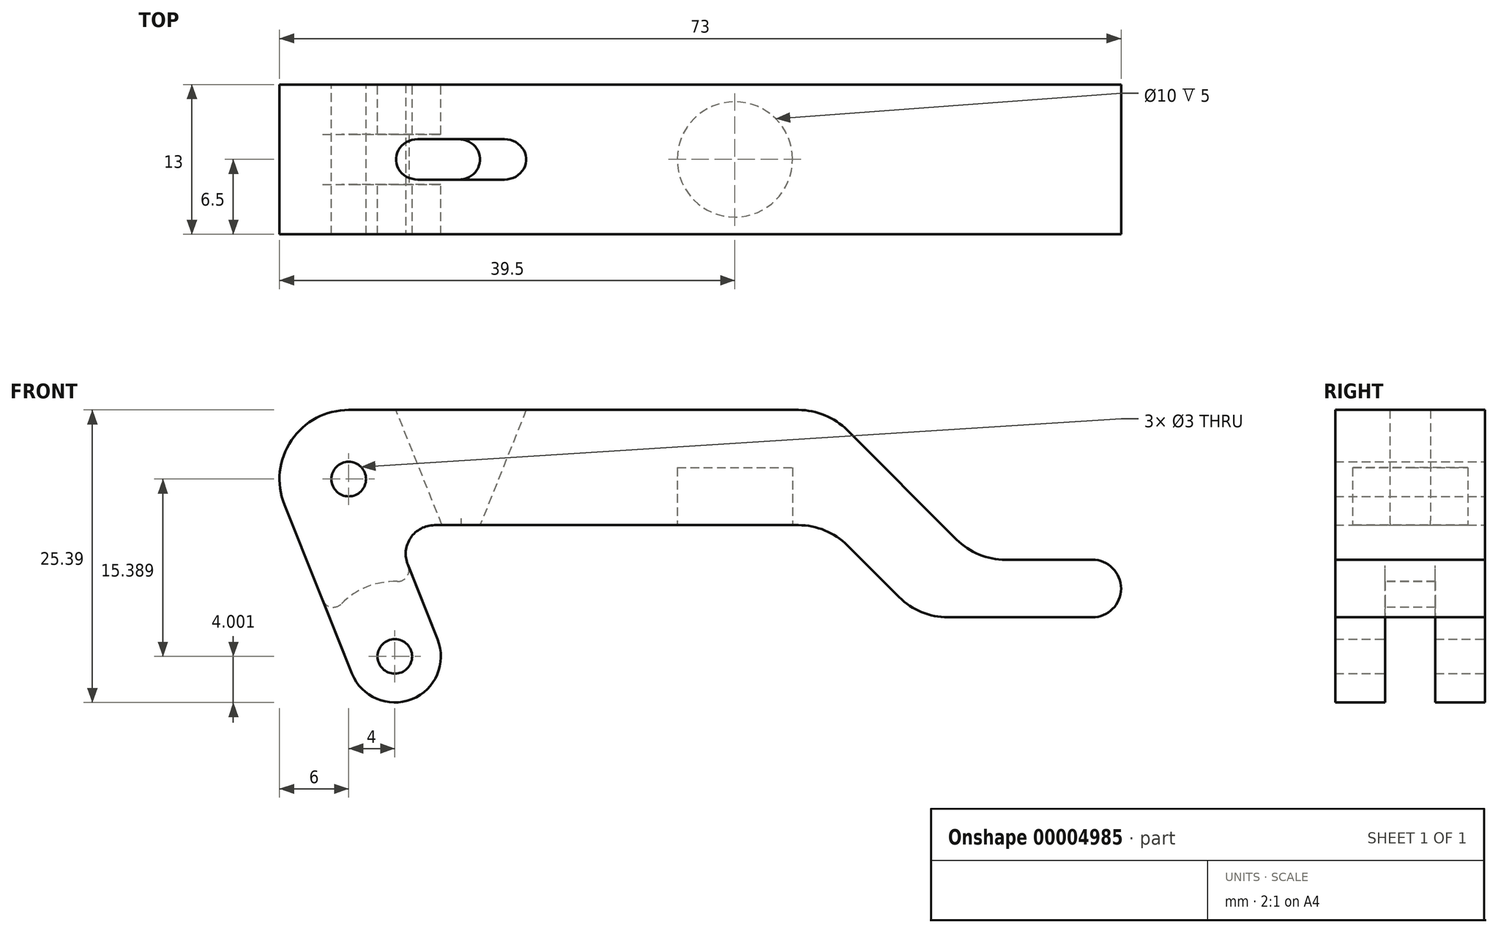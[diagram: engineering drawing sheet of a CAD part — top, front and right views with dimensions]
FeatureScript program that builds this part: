
annotation { "Feature Type Name" : "Feature", "Feature Type Description" : "" }
export const myFeature = defineFeature(function(context is Context, id is Id, definition is map)
    precondition{}
    {
        {
            var Q0;
            Q0=qCreatedBy(makeId("Front.planeOp"),FACE);
            var sketch = newSketch(context, id + "F0", { "sketchPlane" : qUnion([Q0])});
            skLineSegment(sketch, "E0", {"start": v(0, 0) * mm, "end": v(31, 0) * mm, "construction": true});
            skCircle(sketch, "E1", {"center": v(0, 0) * mm, "radius": 1.5 * mm});
            skLineSegment(sketch, "E2", {"start": v(0, 0) * mm, "end": v(4, -15.39) * mm, "construction": true});
            skCircle(sketch, "E3", {"center": v(4, -15.39) * mm, "radius": 1.5 * mm});
            skArc(sketch, "E4", {"start": v(-5.57, -2.23) * mm, "mid": v(-4.97, 3.36) * mm, "end": v(0, 6) * mm});
            skArc(sketch, "E5", {"start": v(0.29, -16.87) * mm, "mid": v(5.49, -19.1) * mm, "end": v(7.71, -13.9) * mm});
            skLineSegment(sketch, "E6", {"start": v(-5.57, -2.23) * mm, "end": v(0.29, -16.87) * mm});
            skLineSegment(sketch, "E7", {"start": v(0, 6) * mm, "end": v(41.5, 6) * mm});
            skLineSegment(sketch, "E8", {"start": v(41.5, 6) * mm, "end": v(54.5, -7) * mm});
            skLineSegment(sketch, "E9", {"start": v(54.5, -7) * mm, "end": v(67, -7) * mm});
            skLineSegment(sketch, "E10", {"start": v(15.5, 0) * mm, "end": v(15.5, -12.95) * mm, "construction": true});
            skLineSegment(sketch, "E11", {"start": v(9.75, 0) * mm, "end": v(9.75, -27.58) * mm, "construction": true});
            skLineSegment(sketch, "E12", {"start": v(7.71, -13.9) * mm, "end": v(3.75, -4) * mm});
            skLineSegment(sketch, "E13", {"start": v(3.75, -4) * mm, "end": v(41.5, -4) * mm});
            skLineSegment(sketch, "E14", {"start": v(41.5, -4) * mm, "end": v(49.5, -12) * mm});
            skLineSegment(sketch, "E15", {"start": v(49.5, -12) * mm, "end": v(67, -12) * mm});
            skLineSegment(sketch, "E16", {"start": v(67, -12) * mm, "end": v(67, -7) * mm});
            skSolve(sketch);
        }
        {
            var Q0;
            Q0 = qSketchRegion(id + "F0", true);
            extrude(context, id + "F1", {"entities" : qUnion([Q0]), "depth" : 13 * mm, "symmetric" : true});
        }
        {
            var Q0;
            Q0=qCreatedBy(makeId("Front.planeOp"),FACE);
            var sketch = newSketch(context, id + "F2", { "sketchPlane" : qUnion([Q0])});
            skCircle(sketch, "E17.0", {"center": v(4, -15.39) * mm, "radius": 1.5 * mm, "construction": true});
            skCircle(sketch, "E18", {"center": v(4, -15.39) * mm, "radius": 6.5 * mm});
            skSolve(sketch);
        }
        {
            var Q0;
            Q0 = qSketchRegion(id + "F2", true);
            extrude(context, id + "F3", {"entities" : qUnion([Q0]), "operationType" : NewBodyOperationType.REMOVE, "oppositeDirection" : true, "depth" : 4.35 * mm, "symmetric" : true});
        }
        {
            var Q0;
            Q0=qCreatedBy(makeId("Front.planeOp"),FACE);
            var sketch = newSketch(context, id + "F4", { "sketchPlane" : qUnion([Q0])});
            skLineSegment(sketch, "E19", {"start": v(0, 0) * mm, "end": v(15.5, 0) * mm, "construction": true});
            skLineSegment(sketch, "E20", {"start": v(9.75, 0) * mm, "end": v(9.75, -20.2) * mm, "construction": true});
            skPoint(sketch, "E21", {"position": v(6.5, 0) * mm});
            skLineSegment(sketch, "E22", {"start": v(8.5, 0) * mm, "end": v(8.5, -21.18) * mm, "construction": true});
            skLineSegment(sketch, "E23.0", {"start": v(0, 6) * mm, "end": v(41.5, 6) * mm, "construction": true});
            skLineSegment(sketch, "E23.1", {"start": v(3.75, -4) * mm, "end": v(41.5, -4) * mm, "construction": true});
            skLineSegment(sketch, "E24", {"start": v(4.1, 6) * mm, "end": v(8.1, -4) * mm});
            skLineSegment(sketch, "E25.MirrorCS", {"start": v(15.4, 6) * mm, "end": v(11.4, -4) * mm});
            skLineSegment(sketch, "E26", {"start": v(4.1, 6) * mm, "end": v(15.4, 6) * mm});
            skLineSegment(sketch, "E27", {"start": v(8.1, -4) * mm, "end": v(11.4, -4) * mm});
            skSolve(sketch);
        }
        {
            var Q0;
            Q0 = qSketchRegion(id + "F4", true);
            extrude(context, id + "F5", {"entities" : qUnion([Q0]), "operationType" : NewBodyOperationType.REMOVE, "depth" : 3.5 * mm, "symmetric" : true});
        }
        {
            var Q0;
            Q0=makeQuery(id+"F1.opExtrude","SWEPT_EDGE",EDGE,{"disambiguationData":[OSD([sQuery(id+"F0.wireOp",EDGE,"E12"),sQuery(id+"F0.wireOp",EDGE,"E13")])]});
            var Q1;
            Q1=makeQuery(id+"F1.opExtrude","SWEPT_EDGE",EDGE,{"disambiguationData":[OSD([sQuery(id+"F0.wireOp",EDGE,"E9"),sQuery(id+"F0.wireOp",EDGE,"E16")])]});
            var Q2;
            Q2=makeQuery(id+"F1.opExtrude","SWEPT_EDGE",EDGE,{"disambiguationData":[OSD([sQuery(id+"F0.wireOp",EDGE,"E15"),sQuery(id+"F0.wireOp",EDGE,"E16")])]});
            fillet(context, id + "F6", {"entities" : qUnion([Q0, Q1, Q2]), "radius" : 2.5 * mm, "tangentPropagation" : true, "allowEdgeOverflow" : false});
        }
        {
            var Q0;
            Q0=makeQuery(id+"F5.boolean.opBoolean","COPY",EDGE,{"derivedFrom":makeQuery(id+"F5.opExtrude","CAP_EDGE",EDGE,{"disambiguationData":[OSD([sQuery(id+"F4.wireOp",EDGE,"E25.MirrorCS")])],"isStart":true})});
            var Q1;
            Q1=makeQuery(id+"F5.boolean.opBoolean","COPY",EDGE,{"derivedFrom":makeQuery(id+"F5.opExtrude","CAP_EDGE",EDGE,{"disambiguationData":[OSD([sQuery(id+"F4.wireOp",EDGE,"E24")])],"isStart":true})});
            var Q2;
            Q2=makeQuery(id+"F5.boolean.opBoolean","COPY",EDGE,{"derivedFrom":makeQuery(id+"F5.opExtrude","CAP_EDGE",EDGE,{"disambiguationData":[OSD([sQuery(id+"F4.wireOp",EDGE,"E25.MirrorCS")])],"isStart":false})});
            var Q3;
            Q3=makeQuery(id+"F5.boolean.opBoolean","COPY",EDGE,{"derivedFrom":makeQuery(id+"F5.opExtrude","CAP_EDGE",EDGE,{"disambiguationData":[OSD([sQuery(id+"F4.wireOp",EDGE,"E24")])],"isStart":false})});
            fillet(context, id + "F7", {"entities" : qUnion([Q0, Q1, Q2, Q3]), "radius" : 1.75 * mm, "tangentPropagation" : true, "allowEdgeOverflow" : false});
        }
        {
            var Q0;
            Q0=makeQuery(id+"F3.boolean.opBoolean","INTERSECT",EDGE,{"derivedFrom":[makeQuery(id+"F1.opExtrude","SWEPT_FACE",FACE,{"disambiguationData":[OSD([sQuery(id+"F0.wireOp",EDGE,"E6")])]}),makeQuery(id+"F3.opExtrude","SWEPT_FACE",FACE,{"disambiguationData":[OSD([sQuery(id+"F2.wireOp",EDGE,"E18")])]})]});
            var Q1;
            Q1=makeQuery(id+"F3.boolean.opBoolean","INTERSECT",EDGE,{"derivedFrom":[makeQuery(id+"F1.opExtrude","SWEPT_FACE",FACE,{"disambiguationData":[OSD([sQuery(id+"F0.wireOp",EDGE,"E12")])]}),makeQuery(id+"F3.opExtrude","SWEPT_FACE",FACE,{"disambiguationData":[OSD([sQuery(id+"F2.wireOp",EDGE,"E18")])]})]});
            fillet(context, id + "F8", {"entities" : qUnion([Q0, Q1]), "radius" : 1 * mm, "tangentPropagation" : true, "allowEdgeOverflow" : false});
        }
        {
            var Q0;
            Q0=makeQuery(id+"F1.opExtrude","SWEPT_EDGE",EDGE,{"disambiguationData":[OSD([sQuery(id+"F0.wireOp",EDGE,"E7"),sQuery(id+"F0.wireOp",EDGE,"E8")])]});
            var Q1;
            Q1=makeQuery(id+"F1.opExtrude","SWEPT_EDGE",EDGE,{"disambiguationData":[OSD([sQuery(id+"F0.wireOp",EDGE,"E8"),sQuery(id+"F0.wireOp",EDGE,"E9")])]});
            var Q2;
            Q2=makeQuery(id+"F1.opExtrude","SWEPT_EDGE",EDGE,{"disambiguationData":[OSD([sQuery(id+"F0.wireOp",EDGE,"E13"),sQuery(id+"F0.wireOp",EDGE,"E14")])]});
            var Q3;
            Q3=makeQuery(id+"F1.opExtrude","SWEPT_EDGE",EDGE,{"disambiguationData":[OSD([sQuery(id+"F0.wireOp",EDGE,"E14"),sQuery(id+"F0.wireOp",EDGE,"E15")])]});
            fillet(context, id + "F9", {"entities" : qUnion([Q0, Q1, Q2, Q3]), "radius" : 6 * mm, "tangentPropagation" : true, "allowEdgeOverflow" : false});
        }
        {
            var Q0;
            Q0=makeQuery(id+"F1.opExtrude","SWEPT_FACE",FACE,{"disambiguationData":[OSD([sQuery(id+"F0.wireOp",EDGE,"E13")])]});
            var sketch = newSketch(context, id + "F10", { "sketchPlane" : qUnion([Q0])});
            skLineSegment(sketch, "E28.0", {"start": v(-1.5, 6.5) * mm, "end": v(1.5, 6.5) * mm, "construction": true});
            skLineSegment(sketch, "E29", {"start": v(0, 6.5) * mm, "end": v(31, 6.5) * mm, "construction": true});
            skLineSegment(sketch, "E30", {"start": v(15.5, 6.5) * mm, "end": v(15.5, -6.5) * mm, "construction": true});
            skLineSegment(sketch, "E31", {"start": v(15.5, 0) * mm, "end": v(33.5, 0) * mm, "construction": true});
            skPoint(sketch, "E31.endSnap0", {"position": v(15.5, 0) * mm});
            skPoint(sketch, "E32", {"position": v(23, 0) * mm});
            skCircle(sketch, "E33", {"center": v(33.5, 0) * mm, "radius": 5 * mm});
            skSolve(sketch);
        }
        {
            var Q0;
            Q0 = qSketchRegion(id + "F10", true);
            extrude(context, id + "F11", {"entities" : qUnion([Q0]), "operationType" : NewBodyOperationType.REMOVE, "oppositeDirection" : true, "depth" : 5 * mm});
        }
    });
